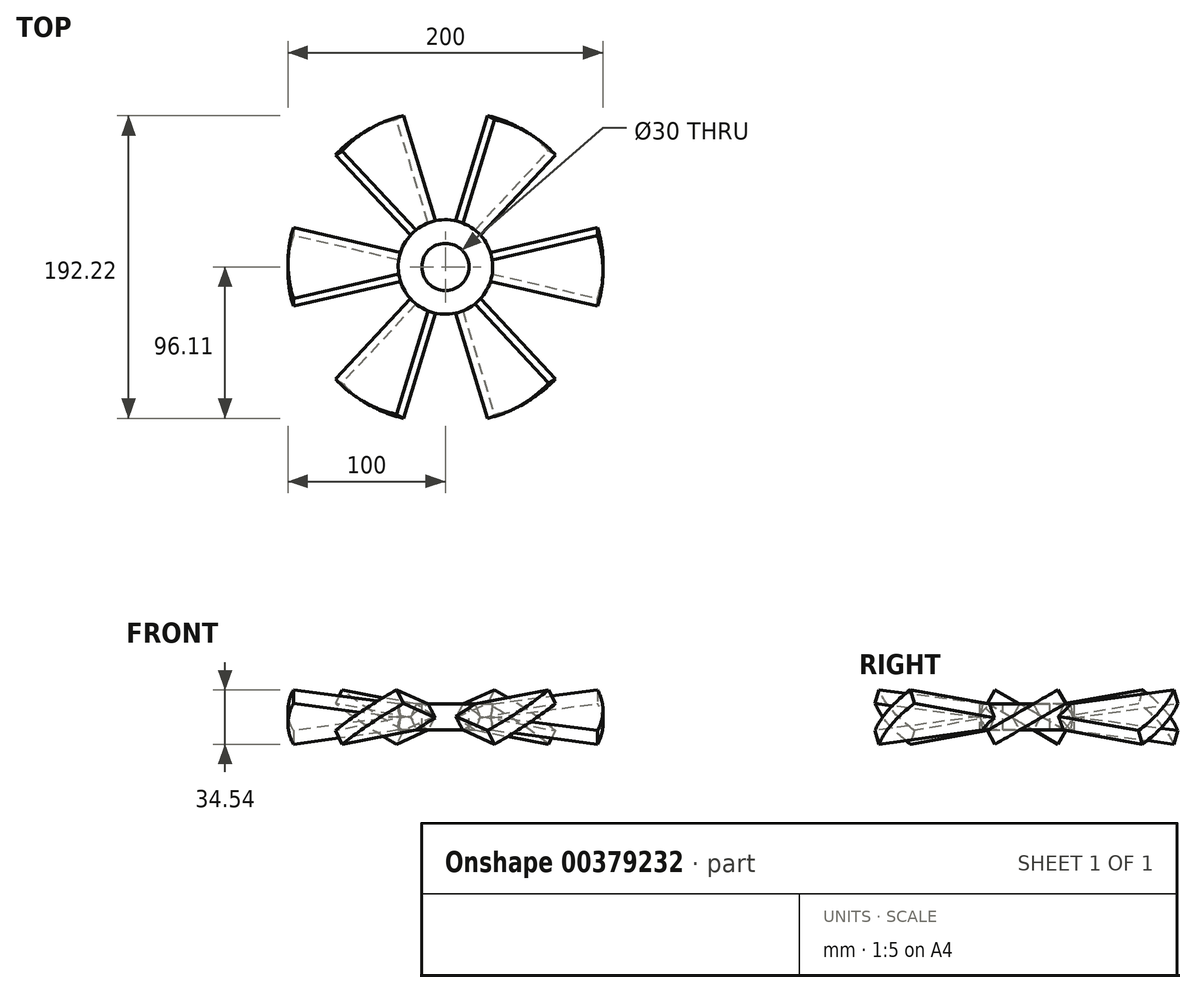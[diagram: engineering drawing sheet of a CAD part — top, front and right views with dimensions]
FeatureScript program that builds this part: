
annotation { "Feature Type Name" : "Feature", "Feature Type Description" : "" }
export const myFeature = defineFeature(function(context is Context, id is Id, definition is map)
    precondition{}
    {
        {
            var Q0;
            Q0=qCreatedBy(makeId("Top.planeOp"),FACE);
            var sketch = newSketch(context, id + "F0", { "sketchPlane" : qUnion([Q0])});
            skLineSegment(sketch, "E0", {"start": v(0, 0) * mm, "end": v(96.6, 25.88) * mm});
            skLineSegment(sketch, "E1", {"start": v(0, 0) * mm, "end": v(96.6, -25.88) * mm});
            skArc(sketch, "E2", {"start": v(96.6, -25.88) * mm, "mid": v(100, 0) * mm, "end": v(96.6, 25.88) * mm});
            skLineSegment(sketch, "E3", {"start": v(96.6, 88.65) * mm, "end": v(96.6, -81.06) * mm, "construction": true});
            skSolve(sketch);
        }
        {
            var Q0;
            Q0 = qSketchRegion(id + "F0", true);
            extrude(context, id + "F1", {"entities" : qUnion([Q0]), "depth" : 5 * mm, "hasSecondDirection" : true, "secondDirectionOppositeDirection" : true, "secondDirectionDepth" : 5 * mm});
        }
        {
            var Q0;
            Q0=qCreatedBy(makeId("Front.planeOp"),FACE);
            var sketch = newSketch(context, id + "F2", { "sketchPlane" : qUnion([Q0])});
            skLineSegment(sketch, "E4", {"start": v(0, 50.42) * mm, "end": v(0, -40.3) * mm, "construction": true});
            skSolve(sketch);
        }
        {
            var Q0;
            Q0=qCreatedBy(makeId("Top.planeOp"),FACE);
            var sketch = newSketch(context, id + "F3", { "sketchPlane" : qUnion([Q0])});
            skLineSegment(sketch, "E5", {"start": v(-45.78, 0) * mm, "end": v(65.73, 0) * mm, "construction": true});
            skSolve(sketch);
        }
        {
            var Q0;
            Q0=makeQuery(id+"F1.opExtrude","SWEPT_BODY",BODY,{"disambiguationData":[OSD([sQuery(id+"F0.wireOp",EDGE,"E0"),sQuery(id+"F0.wireOp",EDGE,"E1"),sQuery(id+"F0.wireOp",EDGE,"E2")])]});
            var Q1;
            Q1=sQuery(id+"F3.wireOp",EDGE,"E5");
            transform(context, id + "F4", {"entities" : qUnion([Q0]), "transformType" : TransformType.ROTATION, "transformAxis" : qUnion([Q1]), "angle" : 30 * degree, "makeCopy" : false});
        }
        {
            var Q0;
            Q0=makeQuery(id+"F1.opExtrude","SWEPT_BODY",BODY,{"disambiguationData":[OSD([sQuery(id+"F0.wireOp",EDGE,"E0"),sQuery(id+"F0.wireOp",EDGE,"E1"),sQuery(id+"F0.wireOp",EDGE,"E2")])]});
            var Q1;
            Q1=sQuery(id+"F2.wireOp",EDGE,"E4");
            circularPattern(context, id + "F5", {"entities" : qUnion([Q0]), "axis" : qUnion([Q1]), "angle" : 360 * degree, "instanceCount" : 6, "equalSpace" : true});
        }
        {
            var Q0;
            Q0=qCreatedBy(makeId("Top.planeOp"),FACE);
            var sketch = newSketch(context, id + "F6", { "sketchPlane" : qUnion([Q0])});
            skCircle(sketch, "E6", {"center": v(0, 0) * mm, "radius": 30 * mm});
            skSolve(sketch);
        }
        {
            var Q0;
            Q0 = qSketchRegion(id + "F6", true);
            extrude(context, id + "F7", {"entities" : qUnion([Q0]), "depth" : 15 * mm, "hasSecondDirection" : true, "secondDirectionOppositeDirection" : true, "secondDirectionDepth" : 15 * mm});
        }
        {
            var Q0;
            Q0=makeQuery(id+"F1.opExtrude","SWEPT_BODY",BODY,{"disambiguationData":[OSD([sQuery(id+"F0.wireOp",EDGE,"E0"),sQuery(id+"F0.wireOp",EDGE,"E1"),sQuery(id+"F0.wireOp",EDGE,"E2")])]});
            var Q1;
            Q1=makeQuery(id+"F5.opPattern","COPY",BODY,{"derivedFrom":makeQuery(id+"F1.opExtrude","SWEPT_BODY",BODY,{"disambiguationData":[OSD([sQuery(id+"F0.wireOp",EDGE,"E0"),sQuery(id+"F0.wireOp",EDGE,"E1"),sQuery(id+"F0.wireOp",EDGE,"E2")])]}),"instanceName":"1"});
            var Q2;
            Q2=makeQuery(id+"F5.opPattern","COPY",BODY,{"derivedFrom":makeQuery(id+"F1.opExtrude","SWEPT_BODY",BODY,{"disambiguationData":[OSD([sQuery(id+"F0.wireOp",EDGE,"E0"),sQuery(id+"F0.wireOp",EDGE,"E1"),sQuery(id+"F0.wireOp",EDGE,"E2")])]}),"instanceName":"2"});
            var Q3;
            Q3=makeQuery(id+"F5.opPattern","COPY",BODY,{"derivedFrom":makeQuery(id+"F1.opExtrude","SWEPT_BODY",BODY,{"disambiguationData":[OSD([sQuery(id+"F0.wireOp",EDGE,"E0"),sQuery(id+"F0.wireOp",EDGE,"E1"),sQuery(id+"F0.wireOp",EDGE,"E2")])]}),"instanceName":"3"});
            var Q4;
            Q4=makeQuery(id+"F5.opPattern","COPY",BODY,{"derivedFrom":makeQuery(id+"F1.opExtrude","SWEPT_BODY",BODY,{"disambiguationData":[OSD([sQuery(id+"F0.wireOp",EDGE,"E0"),sQuery(id+"F0.wireOp",EDGE,"E1"),sQuery(id+"F0.wireOp",EDGE,"E2")])]}),"instanceName":"4"});
            var Q5;
            Q5=makeQuery(id+"F5.opPattern","COPY",BODY,{"derivedFrom":makeQuery(id+"F1.opExtrude","SWEPT_BODY",BODY,{"disambiguationData":[OSD([sQuery(id+"F0.wireOp",EDGE,"E0"),sQuery(id+"F0.wireOp",EDGE,"E1"),sQuery(id+"F0.wireOp",EDGE,"E2")])]}),"instanceName":"5"});
            var Q6;
            Q6=makeQuery(id+"F7.opExtrude","SWEPT_BODY",BODY,{"disambiguationData":[OSD([sQuery(id+"F6.wireOp",EDGE,"E6")])]});
            booleanBodies(context, id + "F8", {"operationType" : BooleanOperationType.UNION, "tools" : qUnion([Q0, Q1, Q2, Q3, Q4, Q5, Q6])});
        }
        {
            var Q0;
            {var subQ0=sQuery(id+"F0.wireOp",EDGE,"E0");Q0=makeQuery(id+"F8.opBoolean","INTERSECT",VERTEX,{"derivedFrom":[makeQuery(id+"F5.opPattern","COPY",FACE,{"derivedFrom":makeQuery(id+"F1.opExtrude","SWEPT_FACE",FACE,{"disambiguationData":[OSD([subQ0])]}),"instanceName":"2"}),makeQuery(id+"F5.opPattern","COPY",FACE,{"derivedFrom":makeQuery(id+"F1.opExtrude","CAP_FACE",FACE,{"disambiguationData":[OSD([subQ0,sQuery(id+"F0.wireOp",EDGE,"E1"),sQuery(id+"F0.wireOp",EDGE,"E2")])],"isStart":false}),"instanceName":"2"}),makeQuery(id+"F7.opExtrude","SWEPT_FACE",FACE,{"disambiguationData":[OSD([sQuery(id+"F6.wireOp",EDGE,"E6")])]})]});}
            var Q1;
            {var subQ0=sQuery(id+"F0.wireOp",EDGE,"E0");Q1=makeQuery(id+"F8.opBoolean","INTERSECT",VERTEX,{"derivedFrom":[makeQuery(id+"F5.opPattern","COPY",FACE,{"derivedFrom":makeQuery(id+"F1.opExtrude","SWEPT_FACE",FACE,{"disambiguationData":[OSD([subQ0])]}),"instanceName":"1"}),makeQuery(id+"F5.opPattern","COPY",FACE,{"derivedFrom":makeQuery(id+"F1.opExtrude","CAP_FACE",FACE,{"disambiguationData":[OSD([subQ0,sQuery(id+"F0.wireOp",EDGE,"E1"),sQuery(id+"F0.wireOp",EDGE,"E2")])],"isStart":false}),"instanceName":"1"}),makeQuery(id+"F7.opExtrude","SWEPT_FACE",FACE,{"disambiguationData":[OSD([sQuery(id+"F6.wireOp",EDGE,"E6")])]})]});}
            var Q2;
            {var subQ0=sQuery(id+"F0.wireOp",EDGE,"E0");Q2=makeQuery(id+"F8.opBoolean","INTERSECT",VERTEX,{"derivedFrom":[makeQuery(id+"F5.opPattern","COPY",FACE,{"derivedFrom":makeQuery(id+"F1.opExtrude","SWEPT_FACE",FACE,{"disambiguationData":[OSD([subQ0])]}),"instanceName":"5"}),makeQuery(id+"F5.opPattern","COPY",FACE,{"derivedFrom":makeQuery(id+"F1.opExtrude","CAP_FACE",FACE,{"disambiguationData":[OSD([subQ0,sQuery(id+"F0.wireOp",EDGE,"E1"),sQuery(id+"F0.wireOp",EDGE,"E2")])],"isStart":false}),"instanceName":"5"}),makeQuery(id+"F7.opExtrude","SWEPT_FACE",FACE,{"disambiguationData":[OSD([sQuery(id+"F6.wireOp",EDGE,"E6")])]})]});}
            cPlane(context, id + "F9", {"entities" : qUnion([Q0, Q1, Q2]), "cplaneType" : CPlaneType.THREE_POINT, "offset" : 25 * mm, "width" : 150 * mm, "height" : 150 * mm});
        }
        {
            var Q0;
            Q0=makeQuery(id+"F7.opExtrude","CAP_FACE",FACE,{"disambiguationData":[OSD([sQuery(id+"F6.wireOp",EDGE,"E6")])],"isStart":false});
            var Q1;
            Q1=qCreatedBy(id+"F9.planeOp",FACE);
            extrude(context, id + "F10", {"entities" : qUnion([Q0]), "operationType" : NewBodyOperationType.REMOVE, "endBound" : BoundingType.UP_TO_SURFACE, "oppositeDirection" : true, "endBoundEntityFace" : qUnion([Q1]), "depth" : 25 * mm});
        }
        {
            var Q0;
            {var subQ0=sQuery(id+"F0.wireOp",EDGE,"E1");Q0=makeQuery(id+"F8.opBoolean","INTERSECT",VERTEX,{"derivedFrom":[makeQuery(id+"F5.opPattern","COPY",FACE,{"derivedFrom":makeQuery(id+"F1.opExtrude","CAP_FACE",FACE,{"disambiguationData":[OSD([sQuery(id+"F0.wireOp",EDGE,"E0"),subQ0,sQuery(id+"F0.wireOp",EDGE,"E2")])],"isStart":true}),"instanceName":"4"}),makeQuery(id+"F5.opPattern","COPY",FACE,{"derivedFrom":makeQuery(id+"F1.opExtrude","SWEPT_FACE",FACE,{"disambiguationData":[OSD([subQ0])]}),"instanceName":"4"}),makeQuery(id+"F7.opExtrude","SWEPT_FACE",FACE,{"disambiguationData":[OSD([sQuery(id+"F6.wireOp",EDGE,"E6")])]})]});}
            var Q1;
            {var subQ0=sQuery(id+"F0.wireOp",EDGE,"E1");Q1=makeQuery(id+"F8.opBoolean","INTERSECT",VERTEX,{"derivedFrom":[makeQuery(id+"F5.opPattern","COPY",FACE,{"derivedFrom":makeQuery(id+"F1.opExtrude","CAP_FACE",FACE,{"disambiguationData":[OSD([sQuery(id+"F0.wireOp",EDGE,"E0"),subQ0,sQuery(id+"F0.wireOp",EDGE,"E2")])],"isStart":true}),"instanceName":"5"}),makeQuery(id+"F5.opPattern","COPY",FACE,{"derivedFrom":makeQuery(id+"F1.opExtrude","SWEPT_FACE",FACE,{"disambiguationData":[OSD([subQ0])]}),"instanceName":"5"}),makeQuery(id+"F7.opExtrude","SWEPT_FACE",FACE,{"disambiguationData":[OSD([sQuery(id+"F6.wireOp",EDGE,"E6")])]})]});}
            var Q2;
            {var subQ0=sQuery(id+"F0.wireOp",EDGE,"E1");Q2=makeQuery(id+"F8.opBoolean","INTERSECT",VERTEX,{"derivedFrom":[makeQuery(id+"F5.opPattern","COPY",FACE,{"derivedFrom":makeQuery(id+"F1.opExtrude","CAP_FACE",FACE,{"disambiguationData":[OSD([sQuery(id+"F0.wireOp",EDGE,"E0"),subQ0,sQuery(id+"F0.wireOp",EDGE,"E2")])],"isStart":true}),"instanceName":"1"}),makeQuery(id+"F5.opPattern","COPY",FACE,{"derivedFrom":makeQuery(id+"F1.opExtrude","SWEPT_FACE",FACE,{"disambiguationData":[OSD([subQ0])]}),"instanceName":"1"}),makeQuery(id+"F7.opExtrude","SWEPT_FACE",FACE,{"disambiguationData":[OSD([sQuery(id+"F6.wireOp",EDGE,"E6")])]})]});}
            cPlane(context, id + "F11", {"entities" : qUnion([Q0, Q1, Q2]), "cplaneType" : CPlaneType.THREE_POINT, "offset" : 25 * mm, "width" : 150 * mm, "height" : 150 * mm});
        }
        {
            var Q0;
            Q0=makeQuery(id+"F7.opExtrude","CAP_FACE",FACE,{"disambiguationData":[OSD([sQuery(id+"F6.wireOp",EDGE,"E6")])],"isStart":true});
            var Q1;
            Q1=qCreatedBy(id+"F11.planeOp",FACE);
            extrude(context, id + "F12", {"entities" : qUnion([Q0]), "operationType" : NewBodyOperationType.REMOVE, "endBound" : BoundingType.UP_TO_SURFACE, "oppositeDirection" : true, "endBoundEntityFace" : qUnion([Q1]), "depth" : 25 * mm});
        }
        {
            var Q0;
            Q0=makeQuery(id+"F10.boolean.opBoolean","COPY",FACE,{"derivedFrom":makeQuery(id+"F10.opExtrude","CAP_FACE",FACE,{"disambiguationData":[OSD([sQuery(id+"F6.wireOp",EDGE,"E6")])],"isStart":false})});
            var sketch = newSketch(context, id + "F13", { "sketchPlane" : qUnion([Q0])});
            skCircle(sketch, "E7", {"center": v(0, 0) * mm, "radius": 15 * mm});
            skSolve(sketch);
        }
        {
            var Q0;
            Q0=makeQuery(id+"F13.imprint","IMPRINT",FACE,{"disambiguationData":[TD([[makeQuery(id+"F13.imprint","IMPRINT",EDGE,{"derivedFrom":sQuery(id+"F13.wireOp",EDGE,"E7")}),1.0]])]});
            extrude(context, id + "F14", {"entities" : qUnion([Q0]), "operationType" : NewBodyOperationType.REMOVE, "oppositeDirection" : true, "depth" : 41.1 * mm});
        }
    });
